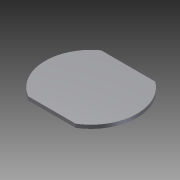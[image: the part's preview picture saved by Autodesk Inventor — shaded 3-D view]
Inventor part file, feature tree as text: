
AUTODESK INVENTOR PART (.ipt)
format: ipt  version: 2012 (Build 160160000, 160)  size: 71,168 bytes
history: native  units: mm
features: extrude x1, sketch x1
ambient origin geometry x8: Origin, YZ Plane, XZ Plane, XY Plane, X Axis, Y Axis, Z Axis, Center Point
bodies: Solid1 (feature_tree)
feature tree (2):
  extrude  "Extrusion1"  Depth=3.0mm TaperAngle=0.0deg
  sketch  "Sketch1"  dims[d2=64.0mm d3=3.0mm d4=0.0mm]
